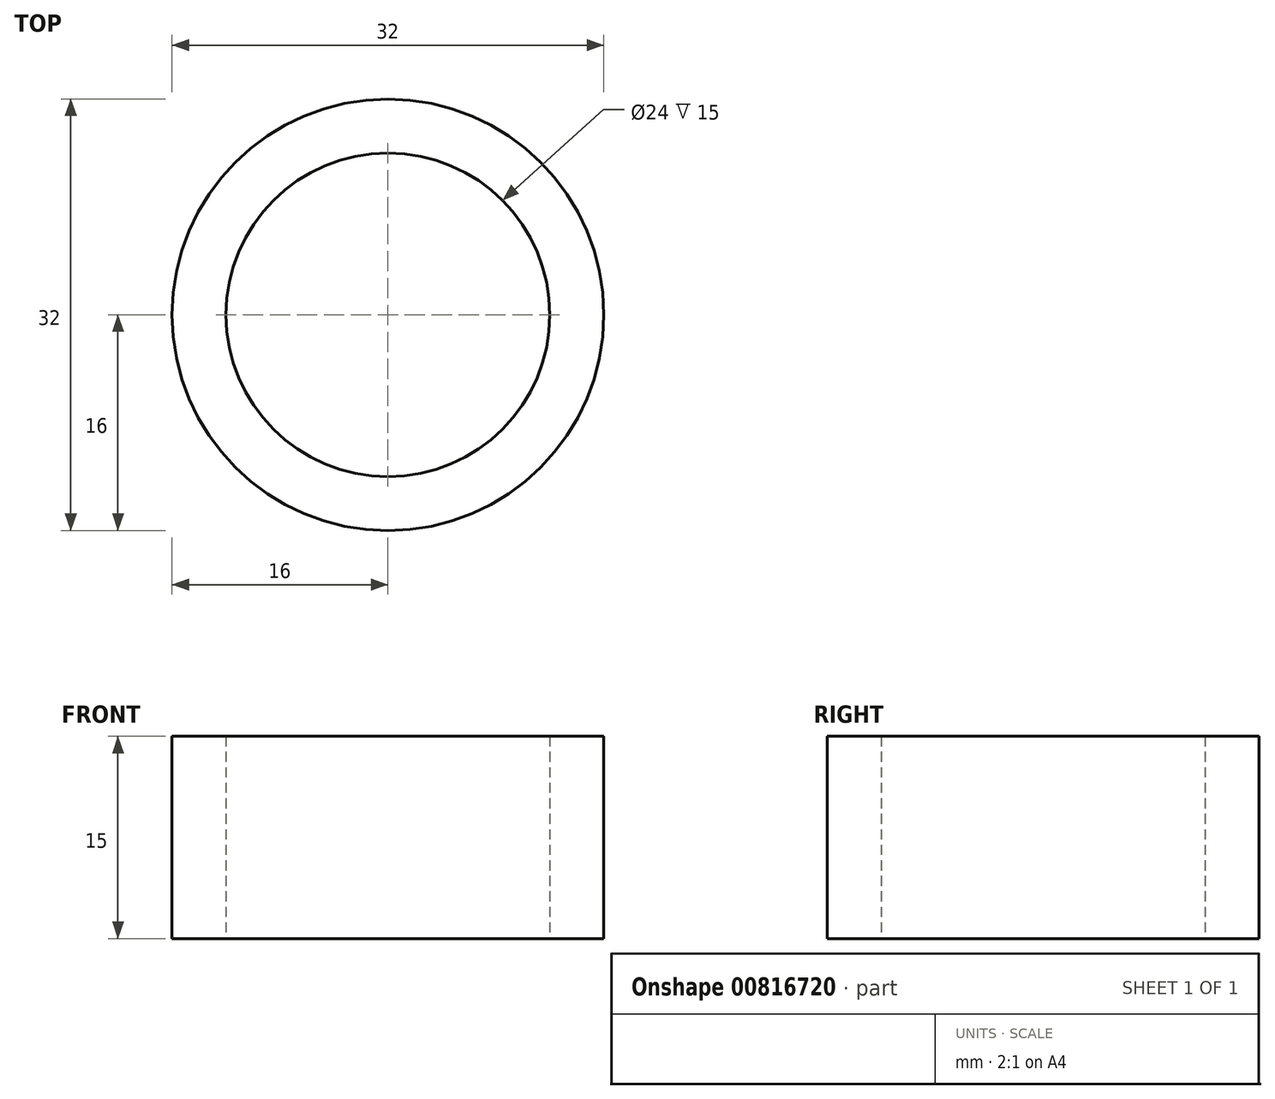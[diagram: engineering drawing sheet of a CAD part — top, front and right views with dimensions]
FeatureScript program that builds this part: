
annotation { "Feature Type Name" : "Feature", "Feature Type Description" : "" }
export const myFeature = defineFeature(function(context is Context, id is Id, definition is map)
    precondition{}
    {
        {
            var Q0;
            Q0=qCreatedBy(makeId("Front.planeOp"),FACE);
            var sketch = newSketch(context, id + "F0", { "sketchPlane" : qUnion([Q0])});
            skLineSegment(sketch, "E0", {"start": v(-12, 0) * mm, "end": v(-12, 15) * mm});
            skLineSegment(sketch, "E1", {"start": v(-12, 15) * mm, "end": v(-16, 15) * mm});
            skLineSegment(sketch, "E2", {"start": v(-16, 15) * mm, "end": v(-16, 0) * mm});
            skLineSegment(sketch, "E3", {"start": v(-16, 0) * mm, "end": v(-12, 0) * mm});
            skLineSegment(sketch, "E4", {"start": v(-12, 0) * mm, "end": v(0, 0) * mm});
            skLineSegment(sketch, "E5", {"start": v(0, 0) * mm, "end": v(0, 15) * mm});
            skSolve(sketch);
        }
        {
            var Q0;
            Q0=makeQuery(id+"F0.imprint","IMPRINT",FACE,{"disambiguationData":[TD([[makeQuery(id+"F0.imprint","IMPRINT",EDGE,{"derivedFrom":sQuery(id+"F0.wireOp",EDGE,"E0")}),1.0]])]});
            var Q1;
            Q1=sQuery(id+"F0.wireOp",EDGE,"E5");
            revolve(context, id + "F1", {"surfaceOperationType" : NewSurfaceOperationType.NEW, "entities" : qUnion([Q0]), "axis" : qUnion([Q1]), "revolveType" : RevolveType.FULL});
        }
    });
